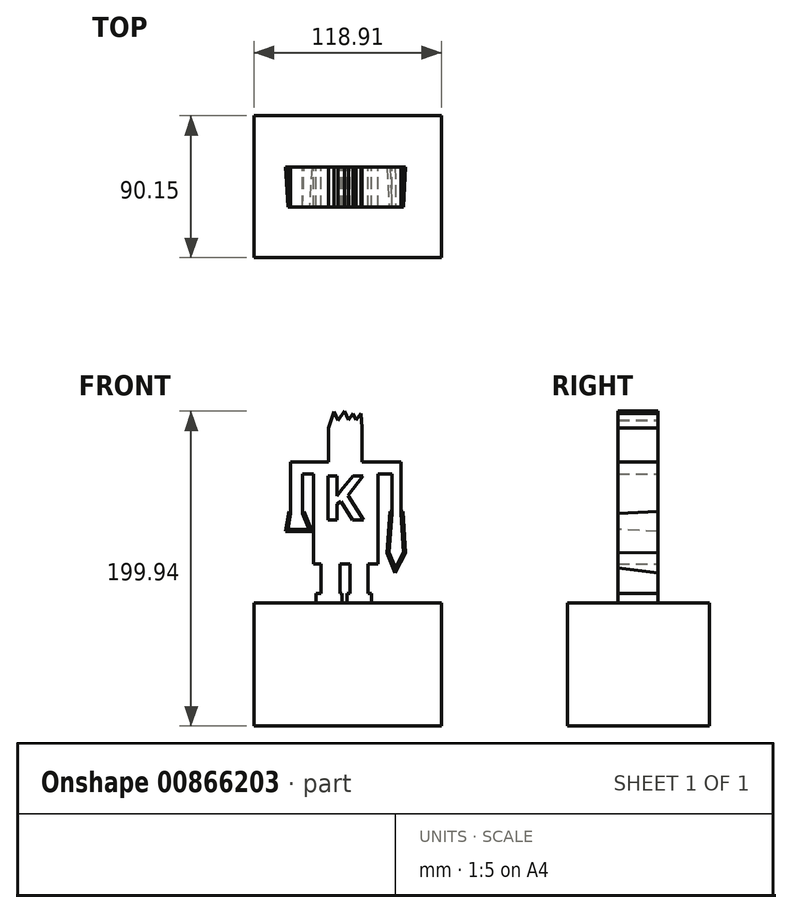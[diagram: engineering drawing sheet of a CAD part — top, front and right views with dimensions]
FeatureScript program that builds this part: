
annotation { "Feature Type Name" : "Feature", "Feature Type Description" : "" }
export const myFeature = defineFeature(function(context is Context, id is Id, definition is map)
    precondition{}
    {
        {
            var Q0;
            Q0=qCreatedBy(makeId("Front.planeOp"),FACE);
            var sketch = newSketch(context, id + "F0", { "sketchPlane" : qUnion([Q0])});
            skLineSegment(sketch, "E0.bottom", {"start": v(-19.63, 37.33) * mm, "end": v(21.3, 37.33) * mm});
            skLineSegment(sketch, "E0.top", {"start": v(-19.63, -27.56) * mm, "end": v(21.3, -27.56) * mm});
            skLineSegment(sketch, "E0.left", {"start": v(-19.63, 37.33) * mm, "end": v(-19.63, -27.56) * mm});
            skLineSegment(sketch, "E0.right", {"start": v(21.3, 37.33) * mm, "end": v(21.3, -27.56) * mm});
            skLineSegment(sketch, "E1", {"start": v(-19.63, 37.33) * mm, "end": v(-34.22, 37.33) * mm});
            skLineSegment(sketch, "E2", {"start": v(-34.22, 37.33) * mm, "end": v(-34.22, 4.52) * mm});
            skLineSegment(sketch, "E3", {"start": v(-34.22, 4.52) * mm, "end": v(-26.62, 4.52) * mm});
            skLineSegment(sketch, "E4", {"start": v(-26.62, 4.52) * mm, "end": v(-26.62, 29.64) * mm});
            skLineSegment(sketch, "E5", {"start": v(-26.62, 29.64) * mm, "end": v(-19.63, 29.64) * mm});
            skLineSegment(sketch, "E6", {"start": v(-19.63, 29.64) * mm, "end": v(-19.63, 37.33) * mm});
            skLineSegment(sketch, "E7", {"start": v(21.3, 37.33) * mm, "end": v(35.85, 37.33) * mm});
            skLineSegment(sketch, "E8", {"start": v(35.85, 37.33) * mm, "end": v(35.85, 4.52) * mm});
            skLineSegment(sketch, "E9", {"start": v(35.85, 4.52) * mm, "end": v(29.96, 4.52) * mm});
            skLineSegment(sketch, "E10", {"start": v(29.96, 4.52) * mm, "end": v(29.96, 29.64) * mm});
            skLineSegment(sketch, "E11", {"start": v(29.96, 29.64) * mm, "end": v(21.3, 29.64) * mm});
            skLineSegment(sketch, "E12", {"start": v(-14.84, -27.56) * mm, "end": v(-14.84, -46.17) * mm});
            skLineSegment(sketch, "E13", {"start": v(-14.84, -46.17) * mm, "end": v(-2.75, -46.17) * mm});
            skLineSegment(sketch, "E14", {"start": v(-2.75, -46.17) * mm, "end": v(-2.75, -27.56) * mm});
            skLineSegment(sketch, "E15", {"start": v(-2.75, -27.56) * mm, "end": v(9.65, -27.56) * mm});
            skLineSegment(sketch, "E16", {"start": v(9.65, -27.56) * mm, "end": v(3.45, -27.56) * mm});
            skLineSegment(sketch, "E17", {"start": v(3.45, -27.56) * mm, "end": v(3.45, -46.17) * mm});
            skLineSegment(sketch, "E18", {"start": v(3.45, -46.17) * mm, "end": v(14.93, -46.17) * mm});
            skLineSegment(sketch, "E19", {"start": v(14.93, -46.17) * mm, "end": v(14.93, -27.56) * mm});
            skLineSegment(sketch, "E20", {"start": v(-18.1, -46.17) * mm, "end": v(-14.84, -46.17) * mm});
            skLineSegment(sketch, "E21", {"start": v(-18.1, -46.17) * mm, "end": v(-18.1, -52.37) * mm});
            skLineSegment(sketch, "E22", {"start": v(-18.1, -52.37) * mm, "end": v(-1.5, -52.37) * mm});
            skLineSegment(sketch, "E23", {"start": v(-1.5, -52.37) * mm, "end": v(-1.5, -46.17) * mm});
            skLineSegment(sketch, "E24", {"start": v(-2.75, -46.17) * mm, "end": v(-1.5, -46.17) * mm});
            skLineSegment(sketch, "E25", {"start": v(3.45, -46.17) * mm, "end": v(1.44, -46.17) * mm});
            skLineSegment(sketch, "E26", {"start": v(1.44, -46.17) * mm, "end": v(1.44, -52.37) * mm});
            skLineSegment(sketch, "E27", {"start": v(1.44, -52.37) * mm, "end": v(16.94, -52.37) * mm});
            skLineSegment(sketch, "E28", {"start": v(16.94, -52.37) * mm, "end": v(16.94, -46.17) * mm});
            skLineSegment(sketch, "E29", {"start": v(16.94, -46.17) * mm, "end": v(14.93, -46.17) * mm});
            skLineSegment(sketch, "E30.bottom", {"start": v(-10.19, 37.33) * mm, "end": v(11.2, 37.33) * mm});
            skLineSegment(sketch, "E30.top", {"start": v(-10.19, 58.73) * mm, "end": v(11.2, 58.73) * mm});
            skLineSegment(sketch, "E30.left", {"start": v(-10.19, 37.33) * mm, "end": v(-10.19, 58.73) * mm});
            skLineSegment(sketch, "E30.right", {"start": v(11.2, 37.33) * mm, "end": v(11.2, 58.73) * mm});
            skLineSegment(sketch, "E31", {"start": v(-10.19, 58.73) * mm, "end": v(-6.73, 69.23) * mm});
            skLineSegment(sketch, "E32", {"start": v(-6.73, 69.23) * mm, "end": v(-4.33, 63.7) * mm});
            skLineSegment(sketch, "E33", {"start": v(-4.33, 63.7) * mm, "end": v(0, 69.6) * mm});
            skLineSegment(sketch, "E34", {"start": v(0, 69.6) * mm, "end": v(2.43, 63.99) * mm});
            skLineSegment(sketch, "E35", {"start": v(2.43, 63.99) * mm, "end": v(5.39, 68.02) * mm});
            skLineSegment(sketch, "E36", {"start": v(5.39, 68.02) * mm, "end": v(7.22, 63.8) * mm});
            skLineSegment(sketch, "E37", {"start": v(7.22, 63.8) * mm, "end": v(10.32, 68.02) * mm});
            skLineSegment(sketch, "E38", {"start": v(10.32, 68.02) * mm, "end": v(11.2, 58.73) * mm});
            skSolve(sketch);
        }
        {
            var Q0;
            Q0 = qSketchRegion(id + "F0", true);
            extrude(context, id + "F1", {"entities" : qUnion([Q0]), "depth" : 25.4 * mm, "offsetDistance" : 25.4 * mm});
        }
        {
            var Q0;
            Q0=makeQuery(id+"F1.opExtrude","CAP_FACE",FACE,{"disambiguationData":[OSD([sQuery(id+"F0.wireOp",EDGE,"E0.bottom"),sQuery(id+"F0.wireOp",EDGE,"E0.top"),sQuery(id+"F0.wireOp",EDGE,"E0.left"),sQuery(id+"F0.wireOp",EDGE,"E0.right"),sQuery(id+"F0.wireOp",EDGE,"E1"),sQuery(id+"F0.wireOp",EDGE,"E2"),sQuery(id+"F0.wireOp",EDGE,"E3"),sQuery(id+"F0.wireOp",EDGE,"E4"),sQuery(id+"F0.wireOp",EDGE,"E5"),sQuery(id+"F0.wireOp",EDGE,"E7"),sQuery(id+"F0.wireOp",EDGE,"E8"),sQuery(id+"F0.wireOp",EDGE,"E9"),sQuery(id+"F0.wireOp",EDGE,"E10"),sQuery(id+"F0.wireOp",EDGE,"E11"),sQuery(id+"F0.wireOp",EDGE,"E12"),sQuery(id+"F0.wireOp",EDGE,"E14"),sQuery(id+"F0.wireOp",EDGE,"E15"),sQuery(id+"F0.wireOp",EDGE,"E17"),sQuery(id+"F0.wireOp",EDGE,"E19"),sQuery(id+"F0.wireOp",EDGE,"E20"),sQuery(id+"F0.wireOp",EDGE,"E21"),sQuery(id+"F0.wireOp",EDGE,"E22"),sQuery(id+"F0.wireOp",EDGE,"E23"),sQuery(id+"F0.wireOp",EDGE,"E24"),sQuery(id+"F0.wireOp",EDGE,"E25"),sQuery(id+"F0.wireOp",EDGE,"E26"),sQuery(id+"F0.wireOp",EDGE,"E27"),sQuery(id+"F0.wireOp",EDGE,"E28"),sQuery(id+"F0.wireOp",EDGE,"E29"),sQuery(id+"F0.wireOp",EDGE,"E30.left"),sQuery(id+"F0.wireOp",EDGE,"E30.right"),sQuery(id+"F0.wireOp",EDGE,"E31"),sQuery(id+"F0.wireOp",EDGE,"E32"),sQuery(id+"F0.wireOp",EDGE,"E33"),sQuery(id+"F0.wireOp",EDGE,"E34"),sQuery(id+"F0.wireOp",EDGE,"E35"),sQuery(id+"F0.wireOp",EDGE,"E36"),sQuery(id+"F0.wireOp",EDGE,"E37"),sQuery(id+"F0.wireOp",EDGE,"E38")])],"isStart":false});
            var sketch = newSketch(context, id + "F2", { "sketchPlane" : qUnion([Q0])});
            skLineSegment(sketch, "E39", {"start": v(29.96, 4.52) * mm, "end": v(28.33, -20.2) * mm});
            skLineSegment(sketch, "E40", {"start": v(28.33, -20.2) * mm, "end": v(32.32, -29.93) * mm});
            skLineSegment(sketch, "E41", {"start": v(32.32, -29.93) * mm, "end": v(37.4, -20.2) * mm});
            skLineSegment(sketch, "E42", {"start": v(37.4, -20.2) * mm, "end": v(35.85, 4.52) * mm});
            skLineSegment(sketch, "E43", {"start": v(35.85, 4.52) * mm, "end": v(32.32, 2.33) * mm});
            skLineSegment(sketch, "E44", {"start": v(32.32, 2.33) * mm, "end": v(29.96, 4.52) * mm});
            skLineSegment(sketch, "E45", {"start": v(-34.22, 4.52) * mm, "end": v(-35.86, -5.62) * mm});
            skLineSegment(sketch, "E46", {"start": v(-35.86, -5.62) * mm, "end": v(-22.58, -5.62) * mm});
            skLineSegment(sketch, "E47", {"start": v(-22.58, -5.62) * mm, "end": v(-26.62, 4.52) * mm});
            skSolve(sketch);
        }
        {
            var Q0;
            Q0 = qSketchRegion(id + "F2", true);
            var Q1;
            Q1=makeQuery(id+"F2.imprint","IMPRINT",FACE,{"disambiguationData":[TD([[makeQuery(id+"F2.imprint","IMPRINT",EDGE,{"derivedFrom":sQuery(id+"F2.wireOp",EDGE,"E45")}),1.0]])]});
            var Q2;
            Q2=makeQuery(id+"F2.imprint","IMPRINT",FACE,{"disambiguationData":[TD([[makeQuery(id+"F2.imprint","IMPRINT",EDGE,{"derivedFrom":sQuery(id+"F2.wireOp",EDGE,"E43")}),-1.0]])]});
            extrude(context, id + "F3", {"entities" : qUnion([Q0, Q1, Q2]), "operationType" : NewBodyOperationType.ADD, "oppositeDirection" : true, "depth" : 25.4 * mm, "offsetDistance" : 25.4 * mm, "hasDraft" : true, "draftAngle" : 3 * degree});
        }
        {
            var Q0;
            Q0=makeQuery(id+"F1.opExtrude","SWEPT_FACE",FACE,{"disambiguationData":[OSD([sQuery(id+"F0.wireOp",EDGE,"E22")])]});
            var sketch = newSketch(context, id + "F4", { "sketchPlane" : qUnion([Q0])});
            skLineSegment(sketch, "E48.bottom", {"start": v(-57.43, 57.43) * mm, "end": v(61.48, 57.43) * mm});
            skLineSegment(sketch, "E48.top", {"start": v(-57.43, -32.72) * mm, "end": v(61.48, -32.72) * mm});
            skLineSegment(sketch, "E48.left", {"start": v(-57.43, 57.43) * mm, "end": v(-57.43, -32.72) * mm});
            skLineSegment(sketch, "E48.right", {"start": v(61.48, 57.43) * mm, "end": v(61.48, -32.72) * mm});
            skSolve(sketch);
        }
        {
            var Q0;
            Q0 = qSketchRegion(id + "F4", true);
            extrude(context, id + "F5", {"entities" : qUnion([Q0]), "operationType" : NewBodyOperationType.ADD, "depth" : 77.98 * mm, "offsetDistance" : 25.4 * mm});
        }
        {
            var Q0;
            {var subQ0=sQuery(id+"F0.wireOp",EDGE,"E3");var subQ1=sQuery(id+"F0.wireOp",EDGE,"E9");Q0=makeQuery(id+"F3.boolean.opBoolean","MERGE",FACE,{"derivedFrom":[makeQuery(id+"F1.opExtrude","CAP_FACE",FACE,{"disambiguationData":[OSD([sQuery(id+"F0.wireOp",EDGE,"E0.bottom"),sQuery(id+"F0.wireOp",EDGE,"E0.top"),sQuery(id+"F0.wireOp",EDGE,"E0.left"),sQuery(id+"F0.wireOp",EDGE,"E0.right"),sQuery(id+"F0.wireOp",EDGE,"E1"),sQuery(id+"F0.wireOp",EDGE,"E2"),subQ0,sQuery(id+"F0.wireOp",EDGE,"E4"),sQuery(id+"F0.wireOp",EDGE,"E5"),sQuery(id+"F0.wireOp",EDGE,"E7"),sQuery(id+"F0.wireOp",EDGE,"E8"),subQ1,sQuery(id+"F0.wireOp",EDGE,"E10"),sQuery(id+"F0.wireOp",EDGE,"E11"),sQuery(id+"F0.wireOp",EDGE,"E12"),sQuery(id+"F0.wireOp",EDGE,"E14"),sQuery(id+"F0.wireOp",EDGE,"E15"),sQuery(id+"F0.wireOp",EDGE,"E17"),sQuery(id+"F0.wireOp",EDGE,"E19"),sQuery(id+"F0.wireOp",EDGE,"E20"),sQuery(id+"F0.wireOp",EDGE,"E21"),sQuery(id+"F0.wireOp",EDGE,"E22"),sQuery(id+"F0.wireOp",EDGE,"E23"),sQuery(id+"F0.wireOp",EDGE,"E24"),sQuery(id+"F0.wireOp",EDGE,"E25"),sQuery(id+"F0.wireOp",EDGE,"E26"),sQuery(id+"F0.wireOp",EDGE,"E27"),sQuery(id+"F0.wireOp",EDGE,"E28"),sQuery(id+"F0.wireOp",EDGE,"E29"),sQuery(id+"F0.wireOp",EDGE,"E30.left"),sQuery(id+"F0.wireOp",EDGE,"E30.right"),sQuery(id+"F0.wireOp",EDGE,"E31"),sQuery(id+"F0.wireOp",EDGE,"E32"),sQuery(id+"F0.wireOp",EDGE,"E33"),sQuery(id+"F0.wireOp",EDGE,"E34"),sQuery(id+"F0.wireOp",EDGE,"E35"),sQuery(id+"F0.wireOp",EDGE,"E36"),sQuery(id+"F0.wireOp",EDGE,"E37"),sQuery(id+"F0.wireOp",EDGE,"E38")])],"isStart":false}),makeQuery(id+"F3.opExtrude","CAP_FACE",FACE,{"disambiguationData":[OSD([subQ1,sQuery(id+"F2.wireOp",EDGE,"E39"),sQuery(id+"F2.wireOp",EDGE,"E40"),sQuery(id+"F2.wireOp",EDGE,"E41"),sQuery(id+"F2.wireOp",EDGE,"E42")])],"isStart":true}),makeQuery(id+"F3.opExtrude","CAP_FACE",FACE,{"disambiguationData":[OSD([subQ0,sQuery(id+"F2.wireOp",EDGE,"E45"),sQuery(id+"F2.wireOp",EDGE,"E46"),sQuery(id+"F2.wireOp",EDGE,"E47")])],"isStart":true})]});}
            var sketch = newSketch(context, id + "F6", { "sketchPlane" : qUnion([Q0])});
            skText(sketch, "E49", { "text": "K", "fontName": "OpenSans-Bold.ttf"});
            const initialGuessF6  = {"E49": [-0.01412, 0.00053, 1, 0, 0.02823]};
            skSetInitialGuess(sketch, initialGuessF6);
            skSolve(sketch);
        }
        {
            var Q0;
            Q0 = qSketchRegion(id + "F6", true);
            extrude(context, id + "F7", {"entities" : qUnion([Q0]), "operationType" : NewBodyOperationType.REMOVE, "oppositeDirection" : true, "depth" : 1 / 203.2 * mm, "offsetDistance" : 25.4 * mm});
        }
    });
